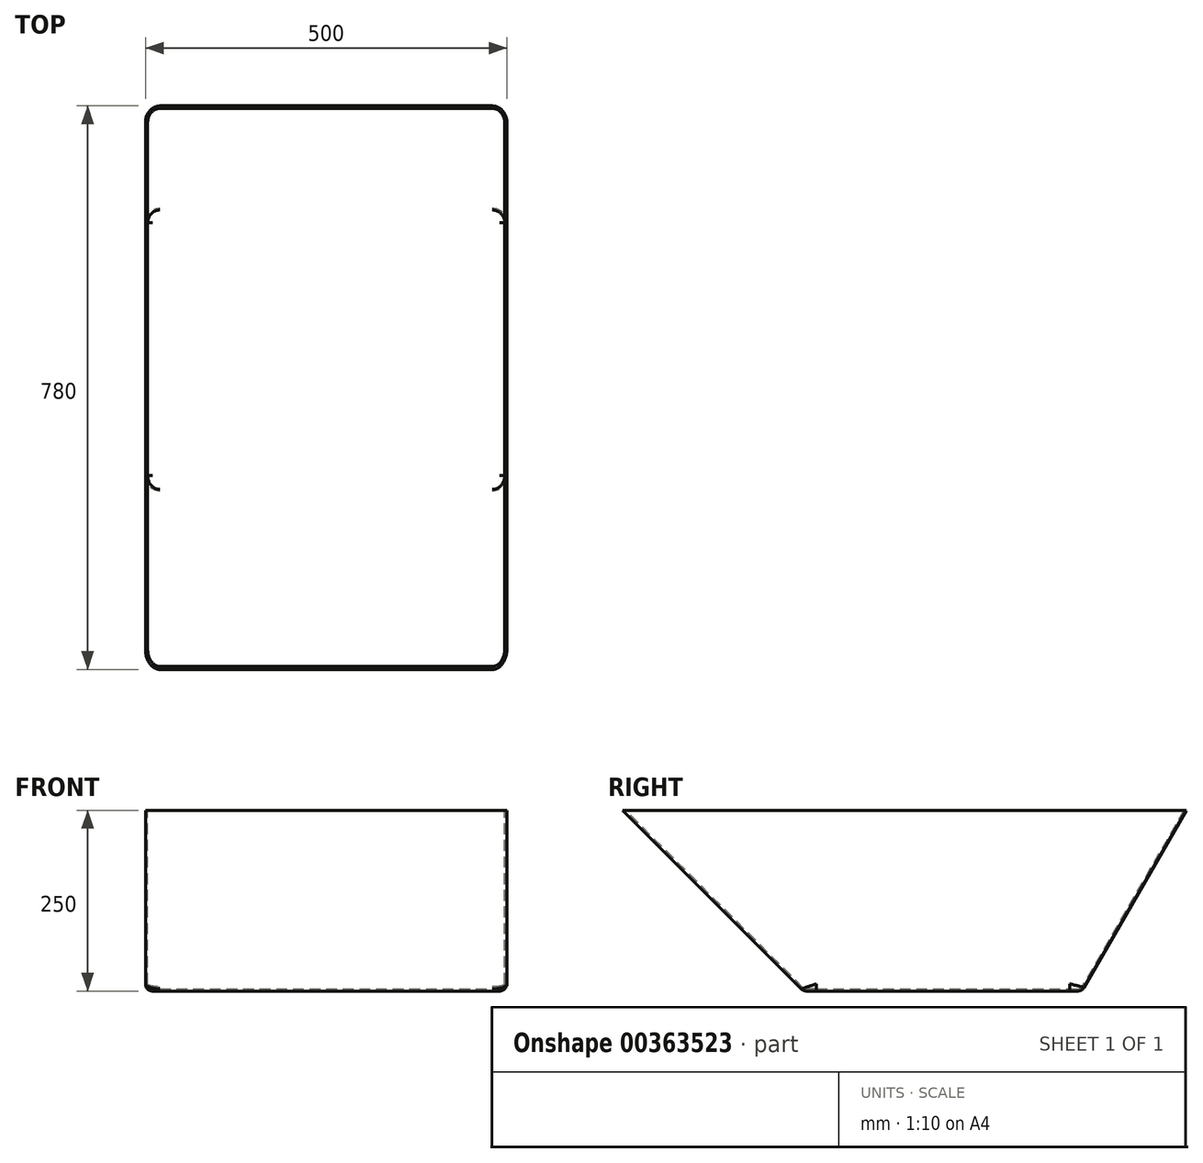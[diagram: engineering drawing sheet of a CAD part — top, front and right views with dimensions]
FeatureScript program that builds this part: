
annotation { "Feature Type Name" : "Feature", "Feature Type Description" : "" }
export const myFeature = defineFeature(function(context is Context, id is Id, definition is map)
    precondition{}
    {
        {
            var Q0;
            Q0=qCreatedBy(makeId("Right.planeOp"),FACE);
            var sketch = newSketch(context, id + "F0", { "sketchPlane" : qUnion([Q0])});
            skLineSegment(sketch, "E0", {"start": v(-192.83, 0) * mm, "end": v(192.83, 0) * mm});
            skLineSegment(sketch, "E1", {"start": v(192.83, 0) * mm, "end": v(337.17, 250) * mm});
            skLineSegment(sketch, "E2", {"start": v(337.17, 250) * mm, "end": v(-442.83, 250) * mm});
            skLineSegment(sketch, "E3", {"start": v(-442.83, 250) * mm, "end": v(-192.83, 0) * mm});
            skSolve(sketch);
        }
        {
            var Q0;
            Q0=makeQuery(id+"F0.imprint","IMPRINT",FACE,{"disambiguationData":[TD([[makeQuery(id+"F0.imprint","IMPRINT",EDGE,{"derivedFrom":sQuery(id+"F0.wireOp",EDGE,"E0")}),1.0]])]});
            extrude(context, id + "F1", {"entities" : qUnion([Q0]), "endBound" : BoundingType.SYMMETRIC, "depth" : 500 * mm});
        }
        {
            var Q0;
            Q0=makeQuery(id+"F1.opExtrude","CAP_EDGE",EDGE,{"disambiguationData":[OSD([sQuery(id+"F0.wireOp",EDGE,"E1")])],"isStart":true});
            var Q1;
            Q1=makeQuery(id+"F1.opExtrude","CAP_EDGE",EDGE,{"disambiguationData":[OSD([sQuery(id+"F0.wireOp",EDGE,"E3")])],"isStart":true});
            var Q2;
            Q2=makeQuery(id+"F1.opExtrude","CAP_EDGE",EDGE,{"disambiguationData":[OSD([sQuery(id+"F0.wireOp",EDGE,"E3")])],"isStart":false});
            var Q3;
            Q3=makeQuery(id+"F1.opExtrude","CAP_EDGE",EDGE,{"disambiguationData":[OSD([sQuery(id+"F0.wireOp",EDGE,"E1")])],"isStart":false});
            fillet(context, id + "F2", {"entities" : qUnion([Q0, Q1, Q2, Q3]), "radius" : 20 * mm, "tangentPropagation" : true, "allowEdgeOverflow" : false});
        }
        {
            var Q0;
            Q0=makeQuery(id+"F1.opExtrude","SWEPT_EDGE",EDGE,{"disambiguationData":[OSD([sQuery(id+"F0.wireOp",EDGE,"E0"),sQuery(id+"F0.wireOp",EDGE,"E3")])]});
            var Q1;
            Q1=makeQuery(id+"F2.opFillet","BLEND_EDGE",EDGE,{"blendedFrom":[makeQuery(id+"F1.opExtrude","CAP_EDGE",EDGE,{"disambiguationData":[OSD([sQuery(id+"F0.wireOp",EDGE,"E3")])],"isStart":false}),makeQuery(id+"F1.opExtrude","SWEPT_FACE",FACE,{"disambiguationData":[OSD([sQuery(id+"F0.wireOp",EDGE,"E0")])]})],"blendedInto":[makeQuery(id+"F1.opExtrude","SWEPT_FACE",FACE,{"disambiguationData":[OSD([sQuery(id+"F0.wireOp",EDGE,"E0")])]})]});
            var Q2;
            Q2=makeQuery(id+"F1.opExtrude","CAP_EDGE",EDGE,{"disambiguationData":[OSD([sQuery(id+"F0.wireOp",EDGE,"E0")])],"isStart":false});
            var Q3;
            Q3=makeQuery(id+"F1.opExtrude","CAP_EDGE",EDGE,{"disambiguationData":[OSD([sQuery(id+"F0.wireOp",EDGE,"E0")])],"isStart":true});
            var Q4;
            Q4=makeQuery(id+"F2.opFillet","BLEND_EDGE",EDGE,{"blendedFrom":[makeQuery(id+"F1.opExtrude","CAP_EDGE",EDGE,{"disambiguationData":[OSD([sQuery(id+"F0.wireOp",EDGE,"E3")])],"isStart":true}),makeQuery(id+"F1.opExtrude","SWEPT_FACE",FACE,{"disambiguationData":[OSD([sQuery(id+"F0.wireOp",EDGE,"E0")])]})],"blendedInto":[makeQuery(id+"F1.opExtrude","SWEPT_FACE",FACE,{"disambiguationData":[OSD([sQuery(id+"F0.wireOp",EDGE,"E0")])]})]});
            var Q5;
            Q5=makeQuery(id+"F1.opExtrude","SWEPT_EDGE",EDGE,{"disambiguationData":[OSD([sQuery(id+"F0.wireOp",EDGE,"E0"),sQuery(id+"F0.wireOp",EDGE,"E1")])]});
            var Q6;
            Q6=makeQuery(id+"F2.opFillet","BLEND_EDGE",EDGE,{"blendedFrom":[makeQuery(id+"F1.opExtrude","CAP_EDGE",EDGE,{"disambiguationData":[OSD([sQuery(id+"F0.wireOp",EDGE,"E1")])],"isStart":false}),makeQuery(id+"F1.opExtrude","SWEPT_FACE",FACE,{"disambiguationData":[OSD([sQuery(id+"F0.wireOp",EDGE,"E0")])]})],"blendedInto":[makeQuery(id+"F1.opExtrude","SWEPT_FACE",FACE,{"disambiguationData":[OSD([sQuery(id+"F0.wireOp",EDGE,"E0")])]})]});
            var Q7;
            Q7=makeQuery(id+"F2.opFillet","BLEND_EDGE",EDGE,{"blendedFrom":[makeQuery(id+"F1.opExtrude","CAP_EDGE",EDGE,{"disambiguationData":[OSD([sQuery(id+"F0.wireOp",EDGE,"E1")])],"isStart":true}),makeQuery(id+"F1.opExtrude","SWEPT_FACE",FACE,{"disambiguationData":[OSD([sQuery(id+"F0.wireOp",EDGE,"E0")])]})],"blendedInto":[makeQuery(id+"F1.opExtrude","SWEPT_FACE",FACE,{"disambiguationData":[OSD([sQuery(id+"F0.wireOp",EDGE,"E0")])]})]});
            fillet(context, id + "F3", {"entities" : qUnion([Q0, Q1, Q2, Q3, Q4, Q5, Q6, Q7]), "radius" : 10 * mm, "tangentPropagation" : true, "allowEdgeOverflow" : false});
        }
        {
            var Q0;
            Q0=makeQuery(id+"F1.opExtrude","SWEPT_FACE",FACE,{"disambiguationData":[OSD([sQuery(id+"F0.wireOp",EDGE,"E2")])]});
            shell(context, id + "F4", {"entities" : qUnion([Q0]), "thickness" : 3 * mm});
        }
    });
